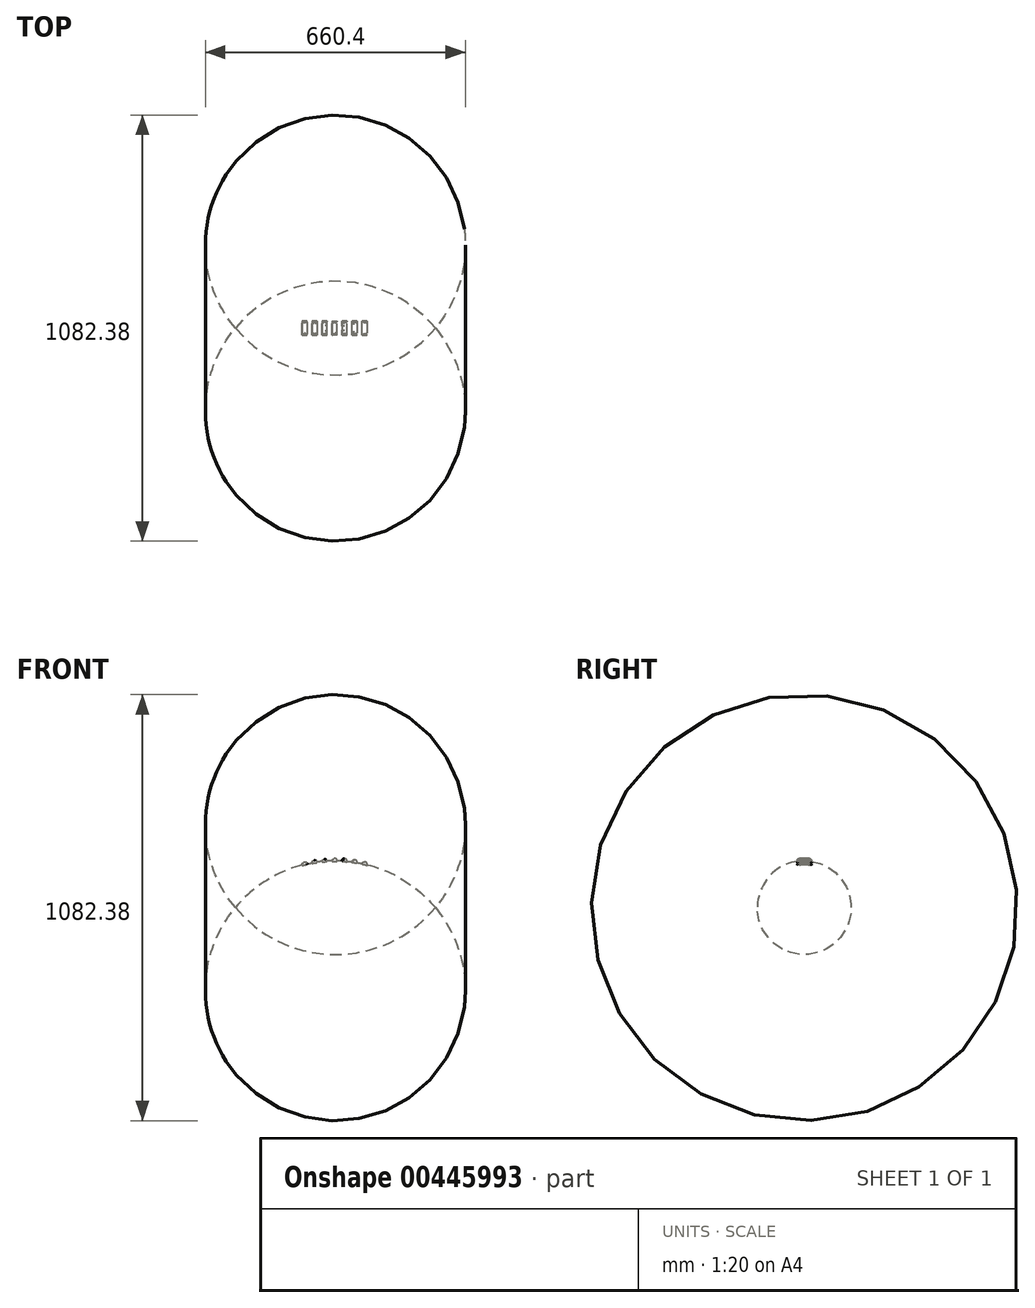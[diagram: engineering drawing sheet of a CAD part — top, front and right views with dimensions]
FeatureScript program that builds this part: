
annotation { "Feature Type Name" : "Feature", "Feature Type Description" : "" }
export const myFeature = defineFeature(function(context is Context, id is Id, definition is map)
    precondition{}
    {
        {
            var Q0;
            Q0=qCreatedBy(makeId("Front.planeOp"),FACE);
            var sketch = newSketch(context, id + "F0", { "sketchPlane" : qUnion([Q0])});
            skLineSegment(sketch, "E0", {"start": v(0, 0) * mm, "end": v(279.4, 0) * mm, "construction": true});
            skArc(sketch, "E1", {"start": v(254, 0) * mm, "mid": v(0, 119.21) * mm, "end": v(-254, 0) * mm});
            skLineSegment(sketch, "E2", {"start": v(-254, 0) * mm, "end": v(254, 0) * mm});
            skSolve(sketch);
        }
        {
            var Q0;
            Q0=makeQuery(id+"F0.imprint","IMPRINT",FACE,{"disambiguationData":[TD([[makeQuery(id+"F0.imprint","IMPRINT",EDGE,{"derivedFrom":sQuery(id+"F0.wireOp",EDGE,"E1")}),1.0]])]});
            var Q1;
            Q1=sQuery(id+"F0.wireOp",EDGE,"E2");
            revolve(context, id + "F1", {"entities" : qUnion([Q0]), "axis" : qUnion([Q1]), "revolveType" : RevolveType.FULL});
        }
        {
            var Q0;
            Q0=qCreatedBy(makeId("Top.planeOp"),FACE);
            cPlane(context, id + "F2", {"entities" : qUnion([Q0]), "cplaneType" : CPlaneType.OFFSET, "offset" : 127 * mm, "width" : 152.4 * mm, "height" : 152.4 * mm});
        }
        {
            var Q0;
            Q0=qCreatedBy(id+"F2.planeOp",FACE);
            var sketch = newSketch(context, id + "F3", { "sketchPlane" : qUnion([Q0])});
            skLineSegment(sketch, "E3", {"start": v(-96.84, 0) * mm, "end": v(80.96, 0) * mm});
            skLineSegment(sketch, "E4", {"start": v(-7.94, 0) * mm, "end": v(-7.94, 17.9) * mm});
            skLineSegment(sketch, "E5", {"start": v(-7.94, 17.9) * mm, "end": v(4.76, 17.9) * mm});
            skLineSegment(sketch, "E6", {"start": v(4.76, 17.9) * mm, "end": v(4.76, 0) * mm});
            skLineSegment(sketch, "E7.1.0.0", {"start": v(17.46, 17.9) * mm, "end": v(30.16, 17.9) * mm});
            skLineSegment(sketch, "E7.1.0.1", {"start": v(30.16, 17.9) * mm, "end": v(30.16, 0) * mm});
            skLineSegment(sketch, "E7.1.0.2", {"start": v(17.46, 0) * mm, "end": v(17.46, 17.9) * mm});
            skLineSegment(sketch, "E7.2.0.0", {"start": v(42.86, 17.9) * mm, "end": v(55.56, 17.9) * mm});
            skLineSegment(sketch, "E7.2.0.1", {"start": v(55.56, 17.9) * mm, "end": v(55.56, 0) * mm});
            skLineSegment(sketch, "E7.2.0.2", {"start": v(42.86, 0) * mm, "end": v(42.86, 17.9) * mm});
            skLineSegment(sketch, "E7.3.0.0", {"start": v(68.26, 17.9) * mm, "end": v(80.96, 17.9) * mm});
            skLineSegment(sketch, "E7.3.0.1", {"start": v(80.96, 17.9) * mm, "end": v(80.96, 0) * mm});
            skLineSegment(sketch, "E7.3.0.2", {"start": v(68.26, 0) * mm, "end": v(68.26, 17.9) * mm});
            skLineSegment(sketch, "E7.direction1", {"start": v(-7.94, 0) * mm, "end": v(17.46, 0) * mm, "construction": true});
            skLineSegment(sketch, "E8.MirrorCS", {"start": v(42.86, 0) * mm, "end": v(42.86, -17.9) * mm});
            skLineSegment(sketch, "E9.MirrorCS", {"start": v(17.46, 0) * mm, "end": v(17.46, -17.9) * mm});
            skLineSegment(sketch, "E10.MirrorCS", {"start": v(30.16, -17.9) * mm, "end": v(30.16, 0) * mm});
            skLineSegment(sketch, "E11.MirrorCS", {"start": v(17.46, -17.9) * mm, "end": v(30.16, -17.9) * mm});
            skLineSegment(sketch, "E12.MirrorCS", {"start": v(-7.94, -17.9) * mm, "end": v(4.76, -17.9) * mm});
            skLineSegment(sketch, "E13.MirrorCS", {"start": v(68.26, -17.9) * mm, "end": v(80.96, -17.9) * mm});
            skLineSegment(sketch, "E14.MirrorCS", {"start": v(4.76, -17.9) * mm, "end": v(4.76, 0) * mm});
            skLineSegment(sketch, "E15.MirrorCS", {"start": v(-7.94, 0) * mm, "end": v(-7.94, -17.9) * mm});
            skLineSegment(sketch, "E16.MirrorCS", {"start": v(80.96, -17.9) * mm, "end": v(80.96, 0) * mm});
            skLineSegment(sketch, "E17.MirrorCS", {"start": v(68.26, 0) * mm, "end": v(68.26, -17.9) * mm});
            skLineSegment(sketch, "E18.MirrorCS", {"start": v(42.86, -17.9) * mm, "end": v(55.56, -17.9) * mm});
            skLineSegment(sketch, "E19.MirrorCS", {"start": v(55.56, -17.9) * mm, "end": v(55.56, 0) * mm});
            skLineSegment(sketch, "E20.1.0.0", {"start": v(-33.34, 17.9) * mm, "end": v(-20.64, 17.9) * mm});
            skLineSegment(sketch, "E20.1.0.1", {"start": v(-20.64, 17.9) * mm, "end": v(-20.64, 0) * mm});
            skLineSegment(sketch, "E20.1.0.2", {"start": v(-33.34, 0) * mm, "end": v(-33.34, 17.9) * mm});
            skLineSegment(sketch, "E20.2.0.0", {"start": v(-58.74, 17.9) * mm, "end": v(-46.04, 17.9) * mm});
            skLineSegment(sketch, "E20.2.0.1", {"start": v(-46.04, 17.9) * mm, "end": v(-46.04, 0) * mm});
            skLineSegment(sketch, "E20.2.0.2", {"start": v(-58.74, 0) * mm, "end": v(-58.74, 17.9) * mm});
            skLineSegment(sketch, "E20.3.0.0", {"start": v(-84.14, 17.9) * mm, "end": v(-71.44, 17.9) * mm});
            skLineSegment(sketch, "E20.3.0.1", {"start": v(-71.44, 17.9) * mm, "end": v(-71.44, 0) * mm});
            skLineSegment(sketch, "E20.3.0.2", {"start": v(-84.14, 0) * mm, "end": v(-84.14, 17.9) * mm});
            skLineSegment(sketch, "E20.direction1", {"start": v(-7.94, 0) * mm, "end": v(-33.34, 0) * mm, "construction": true});
            skLineSegment(sketch, "E21.MirrorCS", {"start": v(-33.34, -17.9) * mm, "end": v(-20.64, -17.9) * mm});
            skLineSegment(sketch, "E22.MirrorCS", {"start": v(-33.34, 0) * mm, "end": v(-33.34, -17.9) * mm});
            skLineSegment(sketch, "E23.MirrorCS", {"start": v(-20.64, -17.9) * mm, "end": v(-20.64, 0) * mm});
            skLineSegment(sketch, "E24.MirrorCS", {"start": v(-58.74, 0) * mm, "end": v(-58.74, -17.9) * mm});
            skLineSegment(sketch, "E25.MirrorCS", {"start": v(-46.04, -17.9) * mm, "end": v(-46.04, 0) * mm});
            skLineSegment(sketch, "E26.MirrorCS", {"start": v(-58.74, -17.9) * mm, "end": v(-46.04, -17.9) * mm});
            skLineSegment(sketch, "E27.MirrorCS", {"start": v(-71.44, -17.9) * mm, "end": v(-71.44, 0) * mm});
            skLineSegment(sketch, "E28.MirrorCS", {"start": v(-84.14, 0) * mm, "end": v(-84.14, -17.9) * mm});
            skLineSegment(sketch, "E29.MirrorCS", {"start": v(-84.14, -17.9) * mm, "end": v(-71.44, -17.9) * mm});
            skSolve(sketch);
        }
        {
            var Q0;
            {var subQ0=sQuery(id+"F3.wireOp",EDGE,"E4");Q0=makeQuery(id+"F3.imprint","IMPRINT",FACE,{"disambiguationData":[TD([[makeQuery(id+"F3.imprint","IMPRINT",EDGE,{"derivedFrom":subQ0}),-1.0]])]});}
            var Q1;
            Q1=makeQuery(id+"F3.imprint","IMPRINT",FACE,{"disambiguationData":[TD([[makeQuery(id+"F3.imprint","IMPRINT",EDGE,{"derivedFrom":sQuery(id+"F3.wireOp",EDGE,"E12.MirrorCS")}),1.0]])]});
            var Q2;
            Q2=makeQuery(id+"F3.imprint","IMPRINT",FACE,{"disambiguationData":[TD([[makeQuery(id+"F3.imprint","IMPRINT",EDGE,{"derivedFrom":sQuery(id+"F3.wireOp",EDGE,"E7.1.0.0")}),-1.0]])]});
            var Q3;
            {var subQ0=sQuery(id+"F3.wireOp",EDGE,"E9.MirrorCS");Q3=makeQuery(id+"F3.imprint","IMPRINT",FACE,{"disambiguationData":[TD([[makeQuery(id+"F3.imprint","IMPRINT",EDGE,{"derivedFrom":subQ0}),1.0]])]});}
            var Q4;
            {var subQ0=sQuery(id+"F3.wireOp",EDGE,"E8.MirrorCS");Q4=makeQuery(id+"F3.imprint","IMPRINT",FACE,{"disambiguationData":[TD([[makeQuery(id+"F3.imprint","IMPRINT",EDGE,{"derivedFrom":subQ0}),1.0]])]});}
            var Q5;
            Q5=makeQuery(id+"F3.imprint","IMPRINT",FACE,{"disambiguationData":[TD([[makeQuery(id+"F3.imprint","IMPRINT",EDGE,{"derivedFrom":sQuery(id+"F3.wireOp",EDGE,"E7.2.0.0")}),-1.0]])]});
            var Q6;
            Q6=makeQuery(id+"F3.imprint","IMPRINT",FACE,{"disambiguationData":[TD([[makeQuery(id+"F3.imprint","IMPRINT",EDGE,{"derivedFrom":sQuery(id+"F3.wireOp",EDGE,"E13.MirrorCS")}),1.0]])]});
            var Q7;
            Q7=makeQuery(id+"F3.imprint","IMPRINT",FACE,{"disambiguationData":[TD([[makeQuery(id+"F3.imprint","IMPRINT",EDGE,{"derivedFrom":sQuery(id+"F3.wireOp",EDGE,"E7.3.0.0")}),-1.0]])]});
            var Q8;
            Q8=makeQuery(id+"F3.imprint","IMPRINT",FACE,{"disambiguationData":[TD([[makeQuery(id+"F3.imprint","IMPRINT",EDGE,{"derivedFrom":sQuery(id+"F3.wireOp",EDGE,"E20.1.0.0")}),-1.0]])]});
            var Q9;
            {var subQ2=sQuery(id+"F3.wireOp",EDGE,"E22.MirrorCS");Q9=makeQuery(id+"F3.imprint","IMPRINT",FACE,{"disambiguationData":[TD([[makeQuery(id+"F3.imprint","IMPRINT",EDGE,{"derivedFrom":subQ2}),1.0]])]});}
            var Q10;
            {var subQ2=sQuery(id+"F3.wireOp",EDGE,"E24.MirrorCS");Q10=makeQuery(id+"F3.imprint","IMPRINT",FACE,{"disambiguationData":[TD([[makeQuery(id+"F3.imprint","IMPRINT",EDGE,{"derivedFrom":subQ2}),1.0]])]});}
            var Q11;
            Q11=makeQuery(id+"F3.imprint","IMPRINT",FACE,{"disambiguationData":[TD([[makeQuery(id+"F3.imprint","IMPRINT",EDGE,{"derivedFrom":sQuery(id+"F3.wireOp",EDGE,"E20.2.0.0")}),-1.0]])]});
            var Q12;
            Q12=makeQuery(id+"F3.imprint","IMPRINT",FACE,{"disambiguationData":[TD([[makeQuery(id+"F3.imprint","IMPRINT",EDGE,{"derivedFrom":sQuery(id+"F3.wireOp",EDGE,"E20.3.0.0")}),-1.0]])]});
            var Q13;
            {var subQ0=sQuery(id+"F3.wireOp",EDGE,"E27.MirrorCS");Q13=makeQuery(id+"F3.imprint","IMPRINT",FACE,{"disambiguationData":[TD([[makeQuery(id+"F3.imprint","IMPRINT",EDGE,{"derivedFrom":subQ0}),1.0]])]});}
            extrude(context, id + "F4", {"entities" : qUnion([Q0, Q1, Q2, Q3, Q4, Q5, Q6, Q7, Q8, Q9, Q10, Q11, Q12, Q13]), "operationType" : NewBodyOperationType.ADD, "endBound" : BoundingType.UP_TO_NEXT, "oppositeDirection" : true, "depth" : 25.4 * mm});
        }
        {
            var Q0;
            Q0=qCreatedBy(makeId("Front.planeOp"),FACE);
            var sketch = newSketch(context, id + "F5", { "sketchPlane" : qUnion([Q0])});
            skArc(sketch, "E30", {"start": v(254.32, 7.54) * mm, "mid": v(0.27, 124.48) * mm, "end": v(-253.78, 7.54) * mm});
            skSolve(sketch);
        }
        {
            var Q0;
            Q0=sQuery(id+"F5.wireOp",EDGE,"E30");
            extrude(context, id + "F6", {"bodyType" : ToolBodyType.SURFACE, "surfaceEntities" : qUnion([Q0]), "endBound" : BoundingType.SYMMETRIC, "depth" : 254 * mm});
        }
        {
            var Q0;
            Q0=qCreatedBy(id+"F2.planeOp",FACE);
            cPlane(context, id + "F7", {"entities" : qUnion([Q0]), "cplaneType" : CPlaneType.OFFSET, "offset" : 25.4 * mm, "width" : 152.4 * mm, "height" : 152.4 * mm});
        }
        {
            var Q0;
            Q0=qCreatedBy(id+"F7.planeOp",FACE);
            var sketch = newSketch(context, id + "F8", { "sketchPlane" : qUnion([Q0])});
            skLineSegment(sketch, "E31.0.0", {"start": v(-84.14, 17.9) * mm, "end": v(-84.14, -17.9) * mm});
            skLineSegment(sketch, "E31.0.1", {"start": v(-84.14, -17.9) * mm, "end": v(-71.44, -17.9) * mm});
            skLineSegment(sketch, "E31.0.2", {"start": v(-71.44, -17.9) * mm, "end": v(-71.44, 17.9) * mm});
            skLineSegment(sketch, "E31.0.3", {"start": v(-71.44, 17.9) * mm, "end": v(-84.14, 17.9) * mm});
            skLineSegment(sketch, "E32.0.0", {"start": v(-58.74, 17.9) * mm, "end": v(-58.74, -17.9) * mm});
            skLineSegment(sketch, "E32.0.1", {"start": v(-58.74, -17.9) * mm, "end": v(-46.04, -17.9) * mm});
            skLineSegment(sketch, "E32.0.2", {"start": v(-46.04, -17.9) * mm, "end": v(-46.04, 17.9) * mm});
            skLineSegment(sketch, "E32.0.3", {"start": v(-46.04, 17.9) * mm, "end": v(-58.74, 17.9) * mm});
            skLineSegment(sketch, "E33.0.0", {"start": v(-33.34, 17.9) * mm, "end": v(-33.34, -17.9) * mm});
            skLineSegment(sketch, "E33.0.1", {"start": v(-33.34, -17.9) * mm, "end": v(-20.64, -17.9) * mm});
            skLineSegment(sketch, "E33.0.2", {"start": v(-20.64, -17.9) * mm, "end": v(-20.64, 17.9) * mm});
            skLineSegment(sketch, "E33.0.3", {"start": v(-20.64, 17.9) * mm, "end": v(-33.34, 17.9) * mm});
            skLineSegment(sketch, "E34.0.0", {"start": v(-7.94, 17.9) * mm, "end": v(-7.94, -17.9) * mm});
            skLineSegment(sketch, "E34.0.1", {"start": v(-7.94, -17.9) * mm, "end": v(4.76, -17.9) * mm});
            skLineSegment(sketch, "E34.0.2", {"start": v(4.76, -17.9) * mm, "end": v(4.76, 17.9) * mm});
            skLineSegment(sketch, "E34.0.3", {"start": v(4.76, 17.9) * mm, "end": v(-7.94, 17.9) * mm});
            skLineSegment(sketch, "E35.0.0", {"start": v(17.46, 17.9) * mm, "end": v(17.46, -17.9) * mm});
            skLineSegment(sketch, "E35.0.1", {"start": v(17.46, -17.9) * mm, "end": v(30.16, -17.9) * mm});
            skLineSegment(sketch, "E35.0.2", {"start": v(30.16, -17.9) * mm, "end": v(30.16, 17.9) * mm});
            skLineSegment(sketch, "E35.0.3", {"start": v(30.16, 17.9) * mm, "end": v(17.46, 17.9) * mm});
            skLineSegment(sketch, "E36.0.0", {"start": v(55.56, -17.9) * mm, "end": v(55.56, 17.9) * mm});
            skLineSegment(sketch, "E36.0.1", {"start": v(55.56, 17.9) * mm, "end": v(42.86, 17.9) * mm});
            skLineSegment(sketch, "E36.0.2", {"start": v(42.86, 17.9) * mm, "end": v(42.86, -17.9) * mm});
            skLineSegment(sketch, "E36.0.3", {"start": v(42.86, -17.9) * mm, "end": v(55.56, -17.9) * mm});
            skLineSegment(sketch, "E37.0.0", {"start": v(80.96, -17.9) * mm, "end": v(80.96, 17.9) * mm});
            skLineSegment(sketch, "E37.0.1", {"start": v(80.96, 17.9) * mm, "end": v(68.26, 17.9) * mm});
            skLineSegment(sketch, "E37.0.2", {"start": v(68.26, 17.9) * mm, "end": v(68.26, -17.9) * mm});
            skLineSegment(sketch, "E37.0.3", {"start": v(68.26, -17.9) * mm, "end": v(80.96, -17.9) * mm});
            skSolve(sketch);
        }
        {
            var Q0;
            Q0=makeQuery(id+"F8.imprint","IMPRINT",FACE,{"disambiguationData":[TD([[makeQuery(id+"F8.imprint","IMPRINT",EDGE,{"derivedFrom":sQuery(id+"F8.wireOp",EDGE,"E31.0.0")}),1.0]])]});
            var Q1;
            Q1=makeQuery(id+"F8.imprint","IMPRINT",FACE,{"disambiguationData":[TD([[makeQuery(id+"F8.imprint","IMPRINT",EDGE,{"derivedFrom":sQuery(id+"F8.wireOp",EDGE,"E32.0.0")}),1.0]])]});
            var Q2;
            Q2=makeQuery(id+"F8.imprint","IMPRINT",FACE,{"disambiguationData":[TD([[makeQuery(id+"F8.imprint","IMPRINT",EDGE,{"derivedFrom":sQuery(id+"F8.wireOp",EDGE,"E33.0.0")}),1.0]])]});
            var Q3;
            Q3=makeQuery(id+"F8.imprint","IMPRINT",FACE,{"disambiguationData":[TD([[makeQuery(id+"F8.imprint","IMPRINT",EDGE,{"derivedFrom":sQuery(id+"F8.wireOp",EDGE,"E34.0.0")}),1.0]])]});
            var Q4;
            Q4=makeQuery(id+"F8.imprint","IMPRINT",FACE,{"disambiguationData":[TD([[makeQuery(id+"F8.imprint","IMPRINT",EDGE,{"derivedFrom":sQuery(id+"F8.wireOp",EDGE,"E35.0.0")}),1.0]])]});
            var Q5;
            Q5=makeQuery(id+"F8.imprint","IMPRINT",FACE,{"disambiguationData":[TD([[makeQuery(id+"F8.imprint","IMPRINT",EDGE,{"derivedFrom":sQuery(id+"F8.wireOp",EDGE,"E36.0.0")}),1.0]])]});
            var Q6;
            Q6=makeQuery(id+"F8.imprint","IMPRINT",FACE,{"disambiguationData":[TD([[makeQuery(id+"F8.imprint","IMPRINT",EDGE,{"derivedFrom":sQuery(id+"F8.wireOp",EDGE,"E37.0.0")}),1.0]])]});
            var Q7;
            Q7=makeQuery(id+"F6.opExtrude","SWEPT_FACE",FACE,{"disambiguationData":[OSD([sQuery(id+"F5.wireOp",EDGE,"E30")])]});
            extrude(context, id + "F9", {"entities" : qUnion([Q0, Q1, Q2, Q3, Q4, Q5, Q6]), "operationType" : NewBodyOperationType.REMOVE, "endBound" : BoundingType.UP_TO_SURFACE, "oppositeDirection" : true, "endBoundEntityFace" : qUnion([Q7]), "depth" : 25.4 * mm});
        }
        {
            var Q0;
            {Q0=qUnion([makeQuery(id+"F9.boolean.opBoolean","COPY",FACE,{"derivedFrom":makeQuery(id+"F9.opExtrude","CAP_FACE",FACE,{"disambiguationData":[OSD([sQuery(id+"F8.wireOp",EDGE,"E33.0.0"),sQuery(id+"F8.wireOp",EDGE,"E33.0.1"),sQuery(id+"F8.wireOp",EDGE,"E33.0.2"),sQuery(id+"F8.wireOp",EDGE,"E33.0.3")])],"isStart":false})}),makeQuery(id+"F9.boolean.opBoolean","COPY",FACE,{"derivedFrom":makeQuery(id+"F9.opExtrude","CAP_FACE",FACE,{"disambiguationData":[OSD([sQuery(id+"F8.wireOp",EDGE,"E34.0.0"),sQuery(id+"F8.wireOp",EDGE,"E34.0.1"),sQuery(id+"F8.wireOp",EDGE,"E34.0.2"),sQuery(id+"F8.wireOp",EDGE,"E34.0.3")])],"isStart":false})}),makeQuery(id+"F9.boolean.opBoolean","COPY",FACE,{"derivedFrom":makeQuery(id+"F9.opExtrude","CAP_FACE",FACE,{"disambiguationData":[OSD([sQuery(id+"F8.wireOp",EDGE,"E37.0.0"),sQuery(id+"F8.wireOp",EDGE,"E37.0.1"),sQuery(id+"F8.wireOp",EDGE,"E37.0.2"),sQuery(id+"F8.wireOp",EDGE,"E37.0.3")])],"isStart":false})}),makeQuery(id+"F9.boolean.opBoolean","COPY",FACE,{"derivedFrom":makeQuery(id+"F9.opExtrude","CAP_FACE",FACE,{"disambiguationData":[OSD([sQuery(id+"F8.wireOp",EDGE,"E31.0.0"),sQuery(id+"F8.wireOp",EDGE,"E31.0.1"),sQuery(id+"F8.wireOp",EDGE,"E31.0.2"),sQuery(id+"F8.wireOp",EDGE,"E31.0.3")])],"isStart":false})}),makeQuery(id+"F9.boolean.opBoolean","COPY",FACE,{"derivedFrom":makeQuery(id+"F9.opExtrude","CAP_FACE",FACE,{"disambiguationData":[OSD([sQuery(id+"F8.wireOp",EDGE,"E35.0.0"),sQuery(id+"F8.wireOp",EDGE,"E35.0.1"),sQuery(id+"F8.wireOp",EDGE,"E35.0.2"),sQuery(id+"F8.wireOp",EDGE,"E35.0.3")])],"isStart":false})}),makeQuery(id+"F9.boolean.opBoolean","COPY",FACE,{"derivedFrom":makeQuery(id+"F9.opExtrude","CAP_FACE",FACE,{"disambiguationData":[OSD([sQuery(id+"F8.wireOp",EDGE,"E32.0.0"),sQuery(id+"F8.wireOp",EDGE,"E32.0.1"),sQuery(id+"F8.wireOp",EDGE,"E32.0.2"),sQuery(id+"F8.wireOp",EDGE,"E32.0.3")])],"isStart":false})}),makeQuery(id+"F9.boolean.opBoolean","COPY",FACE,{"derivedFrom":makeQuery(id+"F9.opExtrude","CAP_FACE",FACE,{"disambiguationData":[OSD([sQuery(id+"F8.wireOp",EDGE,"E36.0.0"),sQuery(id+"F8.wireOp",EDGE,"E36.0.1"),sQuery(id+"F8.wireOp",EDGE,"E36.0.2"),sQuery(id+"F8.wireOp",EDGE,"E36.0.3")])],"isStart":false})})]);}
            var Q1;
            {Q1=qUnion([makeQuery(id+"F9.boolean.opBoolean","COPY",FACE,{"derivedFrom":makeQuery(id+"F9.opExtrude","CAP_FACE",FACE,{"disambiguationData":[OSD([sQuery(id+"F8.wireOp",EDGE,"E33.0.0"),sQuery(id+"F8.wireOp",EDGE,"E33.0.1"),sQuery(id+"F8.wireOp",EDGE,"E33.0.2"),sQuery(id+"F8.wireOp",EDGE,"E33.0.3")])],"isStart":false})}),makeQuery(id+"F9.boolean.opBoolean","COPY",FACE,{"derivedFrom":makeQuery(id+"F9.opExtrude","CAP_FACE",FACE,{"disambiguationData":[OSD([sQuery(id+"F8.wireOp",EDGE,"E34.0.0"),sQuery(id+"F8.wireOp",EDGE,"E34.0.1"),sQuery(id+"F8.wireOp",EDGE,"E34.0.2"),sQuery(id+"F8.wireOp",EDGE,"E34.0.3")])],"isStart":false})}),makeQuery(id+"F9.boolean.opBoolean","COPY",FACE,{"derivedFrom":makeQuery(id+"F9.opExtrude","CAP_FACE",FACE,{"disambiguationData":[OSD([sQuery(id+"F8.wireOp",EDGE,"E37.0.0"),sQuery(id+"F8.wireOp",EDGE,"E37.0.1"),sQuery(id+"F8.wireOp",EDGE,"E37.0.2"),sQuery(id+"F8.wireOp",EDGE,"E37.0.3")])],"isStart":false})}),makeQuery(id+"F9.boolean.opBoolean","COPY",FACE,{"derivedFrom":makeQuery(id+"F9.opExtrude","CAP_FACE",FACE,{"disambiguationData":[OSD([sQuery(id+"F8.wireOp",EDGE,"E31.0.0"),sQuery(id+"F8.wireOp",EDGE,"E31.0.1"),sQuery(id+"F8.wireOp",EDGE,"E31.0.2"),sQuery(id+"F8.wireOp",EDGE,"E31.0.3")])],"isStart":false})}),makeQuery(id+"F9.boolean.opBoolean","COPY",FACE,{"derivedFrom":makeQuery(id+"F9.opExtrude","CAP_FACE",FACE,{"disambiguationData":[OSD([sQuery(id+"F8.wireOp",EDGE,"E35.0.0"),sQuery(id+"F8.wireOp",EDGE,"E35.0.1"),sQuery(id+"F8.wireOp",EDGE,"E35.0.2"),sQuery(id+"F8.wireOp",EDGE,"E35.0.3")])],"isStart":false})}),makeQuery(id+"F9.boolean.opBoolean","COPY",FACE,{"derivedFrom":makeQuery(id+"F9.opExtrude","CAP_FACE",FACE,{"disambiguationData":[OSD([sQuery(id+"F8.wireOp",EDGE,"E32.0.0"),sQuery(id+"F8.wireOp",EDGE,"E32.0.1"),sQuery(id+"F8.wireOp",EDGE,"E32.0.2"),sQuery(id+"F8.wireOp",EDGE,"E32.0.3")])],"isStart":false})}),makeQuery(id+"F9.boolean.opBoolean","COPY",FACE,{"derivedFrom":makeQuery(id+"F9.opExtrude","CAP_FACE",FACE,{"disambiguationData":[OSD([sQuery(id+"F8.wireOp",EDGE,"E36.0.0"),sQuery(id+"F8.wireOp",EDGE,"E36.0.1"),sQuery(id+"F8.wireOp",EDGE,"E36.0.2"),sQuery(id+"F8.wireOp",EDGE,"E36.0.3")])],"isStart":false})})]);}
            var Q2;
            {Q2=qUnion([makeQuery(id+"F9.boolean.opBoolean","COPY",FACE,{"derivedFrom":makeQuery(id+"F9.opExtrude","CAP_FACE",FACE,{"disambiguationData":[OSD([sQuery(id+"F8.wireOp",EDGE,"E33.0.0"),sQuery(id+"F8.wireOp",EDGE,"E33.0.1"),sQuery(id+"F8.wireOp",EDGE,"E33.0.2"),sQuery(id+"F8.wireOp",EDGE,"E33.0.3")])],"isStart":false})}),makeQuery(id+"F9.boolean.opBoolean","COPY",FACE,{"derivedFrom":makeQuery(id+"F9.opExtrude","CAP_FACE",FACE,{"disambiguationData":[OSD([sQuery(id+"F8.wireOp",EDGE,"E34.0.0"),sQuery(id+"F8.wireOp",EDGE,"E34.0.1"),sQuery(id+"F8.wireOp",EDGE,"E34.0.2"),sQuery(id+"F8.wireOp",EDGE,"E34.0.3")])],"isStart":false})}),makeQuery(id+"F9.boolean.opBoolean","COPY",FACE,{"derivedFrom":makeQuery(id+"F9.opExtrude","CAP_FACE",FACE,{"disambiguationData":[OSD([sQuery(id+"F8.wireOp",EDGE,"E37.0.0"),sQuery(id+"F8.wireOp",EDGE,"E37.0.1"),sQuery(id+"F8.wireOp",EDGE,"E37.0.2"),sQuery(id+"F8.wireOp",EDGE,"E37.0.3")])],"isStart":false})}),makeQuery(id+"F9.boolean.opBoolean","COPY",FACE,{"derivedFrom":makeQuery(id+"F9.opExtrude","CAP_FACE",FACE,{"disambiguationData":[OSD([sQuery(id+"F8.wireOp",EDGE,"E31.0.0"),sQuery(id+"F8.wireOp",EDGE,"E31.0.1"),sQuery(id+"F8.wireOp",EDGE,"E31.0.2"),sQuery(id+"F8.wireOp",EDGE,"E31.0.3")])],"isStart":false})}),makeQuery(id+"F9.boolean.opBoolean","COPY",FACE,{"derivedFrom":makeQuery(id+"F9.opExtrude","CAP_FACE",FACE,{"disambiguationData":[OSD([sQuery(id+"F8.wireOp",EDGE,"E35.0.0"),sQuery(id+"F8.wireOp",EDGE,"E35.0.1"),sQuery(id+"F8.wireOp",EDGE,"E35.0.2"),sQuery(id+"F8.wireOp",EDGE,"E35.0.3")])],"isStart":false})}),makeQuery(id+"F9.boolean.opBoolean","COPY",FACE,{"derivedFrom":makeQuery(id+"F9.opExtrude","CAP_FACE",FACE,{"disambiguationData":[OSD([sQuery(id+"F8.wireOp",EDGE,"E32.0.0"),sQuery(id+"F8.wireOp",EDGE,"E32.0.1"),sQuery(id+"F8.wireOp",EDGE,"E32.0.2"),sQuery(id+"F8.wireOp",EDGE,"E32.0.3")])],"isStart":false})}),makeQuery(id+"F9.boolean.opBoolean","COPY",FACE,{"derivedFrom":makeQuery(id+"F9.opExtrude","CAP_FACE",FACE,{"disambiguationData":[OSD([sQuery(id+"F8.wireOp",EDGE,"E36.0.0"),sQuery(id+"F8.wireOp",EDGE,"E36.0.1"),sQuery(id+"F8.wireOp",EDGE,"E36.0.2"),sQuery(id+"F8.wireOp",EDGE,"E36.0.3")])],"isStart":false})})]);}
            var Q3;
            {Q3=qUnion([makeQuery(id+"F9.boolean.opBoolean","COPY",FACE,{"derivedFrom":makeQuery(id+"F9.opExtrude","CAP_FACE",FACE,{"disambiguationData":[OSD([sQuery(id+"F8.wireOp",EDGE,"E33.0.0"),sQuery(id+"F8.wireOp",EDGE,"E33.0.1"),sQuery(id+"F8.wireOp",EDGE,"E33.0.2"),sQuery(id+"F8.wireOp",EDGE,"E33.0.3")])],"isStart":false})}),makeQuery(id+"F9.boolean.opBoolean","COPY",FACE,{"derivedFrom":makeQuery(id+"F9.opExtrude","CAP_FACE",FACE,{"disambiguationData":[OSD([sQuery(id+"F8.wireOp",EDGE,"E34.0.0"),sQuery(id+"F8.wireOp",EDGE,"E34.0.1"),sQuery(id+"F8.wireOp",EDGE,"E34.0.2"),sQuery(id+"F8.wireOp",EDGE,"E34.0.3")])],"isStart":false})}),makeQuery(id+"F9.boolean.opBoolean","COPY",FACE,{"derivedFrom":makeQuery(id+"F9.opExtrude","CAP_FACE",FACE,{"disambiguationData":[OSD([sQuery(id+"F8.wireOp",EDGE,"E37.0.0"),sQuery(id+"F8.wireOp",EDGE,"E37.0.1"),sQuery(id+"F8.wireOp",EDGE,"E37.0.2"),sQuery(id+"F8.wireOp",EDGE,"E37.0.3")])],"isStart":false})}),makeQuery(id+"F9.boolean.opBoolean","COPY",FACE,{"derivedFrom":makeQuery(id+"F9.opExtrude","CAP_FACE",FACE,{"disambiguationData":[OSD([sQuery(id+"F8.wireOp",EDGE,"E31.0.0"),sQuery(id+"F8.wireOp",EDGE,"E31.0.1"),sQuery(id+"F8.wireOp",EDGE,"E31.0.2"),sQuery(id+"F8.wireOp",EDGE,"E31.0.3")])],"isStart":false})}),makeQuery(id+"F9.boolean.opBoolean","COPY",FACE,{"derivedFrom":makeQuery(id+"F9.opExtrude","CAP_FACE",FACE,{"disambiguationData":[OSD([sQuery(id+"F8.wireOp",EDGE,"E35.0.0"),sQuery(id+"F8.wireOp",EDGE,"E35.0.1"),sQuery(id+"F8.wireOp",EDGE,"E35.0.2"),sQuery(id+"F8.wireOp",EDGE,"E35.0.3")])],"isStart":false})}),makeQuery(id+"F9.boolean.opBoolean","COPY",FACE,{"derivedFrom":makeQuery(id+"F9.opExtrude","CAP_FACE",FACE,{"disambiguationData":[OSD([sQuery(id+"F8.wireOp",EDGE,"E32.0.0"),sQuery(id+"F8.wireOp",EDGE,"E32.0.1"),sQuery(id+"F8.wireOp",EDGE,"E32.0.2"),sQuery(id+"F8.wireOp",EDGE,"E32.0.3")])],"isStart":false})}),makeQuery(id+"F9.boolean.opBoolean","COPY",FACE,{"derivedFrom":makeQuery(id+"F9.opExtrude","CAP_FACE",FACE,{"disambiguationData":[OSD([sQuery(id+"F8.wireOp",EDGE,"E36.0.0"),sQuery(id+"F8.wireOp",EDGE,"E36.0.1"),sQuery(id+"F8.wireOp",EDGE,"E36.0.2"),sQuery(id+"F8.wireOp",EDGE,"E36.0.3")])],"isStart":false})})]);}
            var Q4;
            {Q4=qUnion([makeQuery(id+"F9.boolean.opBoolean","COPY",FACE,{"derivedFrom":makeQuery(id+"F9.opExtrude","CAP_FACE",FACE,{"disambiguationData":[OSD([sQuery(id+"F8.wireOp",EDGE,"E33.0.0"),sQuery(id+"F8.wireOp",EDGE,"E33.0.1"),sQuery(id+"F8.wireOp",EDGE,"E33.0.2"),sQuery(id+"F8.wireOp",EDGE,"E33.0.3")])],"isStart":false})}),makeQuery(id+"F9.boolean.opBoolean","COPY",FACE,{"derivedFrom":makeQuery(id+"F9.opExtrude","CAP_FACE",FACE,{"disambiguationData":[OSD([sQuery(id+"F8.wireOp",EDGE,"E34.0.0"),sQuery(id+"F8.wireOp",EDGE,"E34.0.1"),sQuery(id+"F8.wireOp",EDGE,"E34.0.2"),sQuery(id+"F8.wireOp",EDGE,"E34.0.3")])],"isStart":false})}),makeQuery(id+"F9.boolean.opBoolean","COPY",FACE,{"derivedFrom":makeQuery(id+"F9.opExtrude","CAP_FACE",FACE,{"disambiguationData":[OSD([sQuery(id+"F8.wireOp",EDGE,"E37.0.0"),sQuery(id+"F8.wireOp",EDGE,"E37.0.1"),sQuery(id+"F8.wireOp",EDGE,"E37.0.2"),sQuery(id+"F8.wireOp",EDGE,"E37.0.3")])],"isStart":false})}),makeQuery(id+"F9.boolean.opBoolean","COPY",FACE,{"derivedFrom":makeQuery(id+"F9.opExtrude","CAP_FACE",FACE,{"disambiguationData":[OSD([sQuery(id+"F8.wireOp",EDGE,"E31.0.0"),sQuery(id+"F8.wireOp",EDGE,"E31.0.1"),sQuery(id+"F8.wireOp",EDGE,"E31.0.2"),sQuery(id+"F8.wireOp",EDGE,"E31.0.3")])],"isStart":false})}),makeQuery(id+"F9.boolean.opBoolean","COPY",FACE,{"derivedFrom":makeQuery(id+"F9.opExtrude","CAP_FACE",FACE,{"disambiguationData":[OSD([sQuery(id+"F8.wireOp",EDGE,"E35.0.0"),sQuery(id+"F8.wireOp",EDGE,"E35.0.1"),sQuery(id+"F8.wireOp",EDGE,"E35.0.2"),sQuery(id+"F8.wireOp",EDGE,"E35.0.3")])],"isStart":false})}),makeQuery(id+"F9.boolean.opBoolean","COPY",FACE,{"derivedFrom":makeQuery(id+"F9.opExtrude","CAP_FACE",FACE,{"disambiguationData":[OSD([sQuery(id+"F8.wireOp",EDGE,"E32.0.0"),sQuery(id+"F8.wireOp",EDGE,"E32.0.1"),sQuery(id+"F8.wireOp",EDGE,"E32.0.2"),sQuery(id+"F8.wireOp",EDGE,"E32.0.3")])],"isStart":false})}),makeQuery(id+"F9.boolean.opBoolean","COPY",FACE,{"derivedFrom":makeQuery(id+"F9.opExtrude","CAP_FACE",FACE,{"disambiguationData":[OSD([sQuery(id+"F8.wireOp",EDGE,"E36.0.0"),sQuery(id+"F8.wireOp",EDGE,"E36.0.1"),sQuery(id+"F8.wireOp",EDGE,"E36.0.2"),sQuery(id+"F8.wireOp",EDGE,"E36.0.3")])],"isStart":false})})]);}
            var Q5;
            {Q5=qUnion([makeQuery(id+"F9.boolean.opBoolean","COPY",FACE,{"derivedFrom":makeQuery(id+"F9.opExtrude","CAP_FACE",FACE,{"disambiguationData":[OSD([sQuery(id+"F8.wireOp",EDGE,"E33.0.0"),sQuery(id+"F8.wireOp",EDGE,"E33.0.1"),sQuery(id+"F8.wireOp",EDGE,"E33.0.2"),sQuery(id+"F8.wireOp",EDGE,"E33.0.3")])],"isStart":false})}),makeQuery(id+"F9.boolean.opBoolean","COPY",FACE,{"derivedFrom":makeQuery(id+"F9.opExtrude","CAP_FACE",FACE,{"disambiguationData":[OSD([sQuery(id+"F8.wireOp",EDGE,"E34.0.0"),sQuery(id+"F8.wireOp",EDGE,"E34.0.1"),sQuery(id+"F8.wireOp",EDGE,"E34.0.2"),sQuery(id+"F8.wireOp",EDGE,"E34.0.3")])],"isStart":false})}),makeQuery(id+"F9.boolean.opBoolean","COPY",FACE,{"derivedFrom":makeQuery(id+"F9.opExtrude","CAP_FACE",FACE,{"disambiguationData":[OSD([sQuery(id+"F8.wireOp",EDGE,"E37.0.0"),sQuery(id+"F8.wireOp",EDGE,"E37.0.1"),sQuery(id+"F8.wireOp",EDGE,"E37.0.2"),sQuery(id+"F8.wireOp",EDGE,"E37.0.3")])],"isStart":false})}),makeQuery(id+"F9.boolean.opBoolean","COPY",FACE,{"derivedFrom":makeQuery(id+"F9.opExtrude","CAP_FACE",FACE,{"disambiguationData":[OSD([sQuery(id+"F8.wireOp",EDGE,"E31.0.0"),sQuery(id+"F8.wireOp",EDGE,"E31.0.1"),sQuery(id+"F8.wireOp",EDGE,"E31.0.2"),sQuery(id+"F8.wireOp",EDGE,"E31.0.3")])],"isStart":false})}),makeQuery(id+"F9.boolean.opBoolean","COPY",FACE,{"derivedFrom":makeQuery(id+"F9.opExtrude","CAP_FACE",FACE,{"disambiguationData":[OSD([sQuery(id+"F8.wireOp",EDGE,"E35.0.0"),sQuery(id+"F8.wireOp",EDGE,"E35.0.1"),sQuery(id+"F8.wireOp",EDGE,"E35.0.2"),sQuery(id+"F8.wireOp",EDGE,"E35.0.3")])],"isStart":false})}),makeQuery(id+"F9.boolean.opBoolean","COPY",FACE,{"derivedFrom":makeQuery(id+"F9.opExtrude","CAP_FACE",FACE,{"disambiguationData":[OSD([sQuery(id+"F8.wireOp",EDGE,"E32.0.0"),sQuery(id+"F8.wireOp",EDGE,"E32.0.1"),sQuery(id+"F8.wireOp",EDGE,"E32.0.2"),sQuery(id+"F8.wireOp",EDGE,"E32.0.3")])],"isStart":false})}),makeQuery(id+"F9.boolean.opBoolean","COPY",FACE,{"derivedFrom":makeQuery(id+"F9.opExtrude","CAP_FACE",FACE,{"disambiguationData":[OSD([sQuery(id+"F8.wireOp",EDGE,"E36.0.0"),sQuery(id+"F8.wireOp",EDGE,"E36.0.1"),sQuery(id+"F8.wireOp",EDGE,"E36.0.2"),sQuery(id+"F8.wireOp",EDGE,"E36.0.3")])],"isStart":false})})]);}
            var Q6;
            {Q6=qUnion([makeQuery(id+"F9.boolean.opBoolean","COPY",FACE,{"derivedFrom":makeQuery(id+"F9.opExtrude","CAP_FACE",FACE,{"disambiguationData":[OSD([sQuery(id+"F8.wireOp",EDGE,"E33.0.0"),sQuery(id+"F8.wireOp",EDGE,"E33.0.1"),sQuery(id+"F8.wireOp",EDGE,"E33.0.2"),sQuery(id+"F8.wireOp",EDGE,"E33.0.3")])],"isStart":false})}),makeQuery(id+"F9.boolean.opBoolean","COPY",FACE,{"derivedFrom":makeQuery(id+"F9.opExtrude","CAP_FACE",FACE,{"disambiguationData":[OSD([sQuery(id+"F8.wireOp",EDGE,"E34.0.0"),sQuery(id+"F8.wireOp",EDGE,"E34.0.1"),sQuery(id+"F8.wireOp",EDGE,"E34.0.2"),sQuery(id+"F8.wireOp",EDGE,"E34.0.3")])],"isStart":false})}),makeQuery(id+"F9.boolean.opBoolean","COPY",FACE,{"derivedFrom":makeQuery(id+"F9.opExtrude","CAP_FACE",FACE,{"disambiguationData":[OSD([sQuery(id+"F8.wireOp",EDGE,"E37.0.0"),sQuery(id+"F8.wireOp",EDGE,"E37.0.1"),sQuery(id+"F8.wireOp",EDGE,"E37.0.2"),sQuery(id+"F8.wireOp",EDGE,"E37.0.3")])],"isStart":false})}),makeQuery(id+"F9.boolean.opBoolean","COPY",FACE,{"derivedFrom":makeQuery(id+"F9.opExtrude","CAP_FACE",FACE,{"disambiguationData":[OSD([sQuery(id+"F8.wireOp",EDGE,"E31.0.0"),sQuery(id+"F8.wireOp",EDGE,"E31.0.1"),sQuery(id+"F8.wireOp",EDGE,"E31.0.2"),sQuery(id+"F8.wireOp",EDGE,"E31.0.3")])],"isStart":false})}),makeQuery(id+"F9.boolean.opBoolean","COPY",FACE,{"derivedFrom":makeQuery(id+"F9.opExtrude","CAP_FACE",FACE,{"disambiguationData":[OSD([sQuery(id+"F8.wireOp",EDGE,"E35.0.0"),sQuery(id+"F8.wireOp",EDGE,"E35.0.1"),sQuery(id+"F8.wireOp",EDGE,"E35.0.2"),sQuery(id+"F8.wireOp",EDGE,"E35.0.3")])],"isStart":false})}),makeQuery(id+"F9.boolean.opBoolean","COPY",FACE,{"derivedFrom":makeQuery(id+"F9.opExtrude","CAP_FACE",FACE,{"disambiguationData":[OSD([sQuery(id+"F8.wireOp",EDGE,"E32.0.0"),sQuery(id+"F8.wireOp",EDGE,"E32.0.1"),sQuery(id+"F8.wireOp",EDGE,"E32.0.2"),sQuery(id+"F8.wireOp",EDGE,"E32.0.3")])],"isStart":false})}),makeQuery(id+"F9.boolean.opBoolean","COPY",FACE,{"derivedFrom":makeQuery(id+"F9.opExtrude","CAP_FACE",FACE,{"disambiguationData":[OSD([sQuery(id+"F8.wireOp",EDGE,"E36.0.0"),sQuery(id+"F8.wireOp",EDGE,"E36.0.1"),sQuery(id+"F8.wireOp",EDGE,"E36.0.2"),sQuery(id+"F8.wireOp",EDGE,"E36.0.3")])],"isStart":false})})]);}
            fillet(context, id + "F10", {"entities" : qUnion([Q0, Q1, Q2, Q3, Q4, Q5, Q6]), "radius" : 5.08 * mm, "tangentPropagation" : true, "allowEdgeOverflow" : false});
        }
    });
